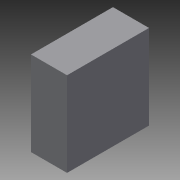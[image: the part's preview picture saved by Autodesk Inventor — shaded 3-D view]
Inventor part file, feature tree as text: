
AUTODESK INVENTOR PART (.ipt)
format: ipt  version: 2015 (Build 190159000, 159)  size: 68,608 bytes
history: native  units: mm
features: extrude x1, sketch x1
ambient origin geometry x8: Origin, YZ Plane, XZ Plane, XY Plane, X Axis, Y Axis, Z Axis, Center Point
bodies: Solid1 (feature_tree)
feature tree (2):
  extrude  "Extrusion1"  Depth=79.5mm
  sketch  "Sketch1"  dims[d0=82.0mm d1=79.5mm d2=35.0mm d3=0.0mm]
